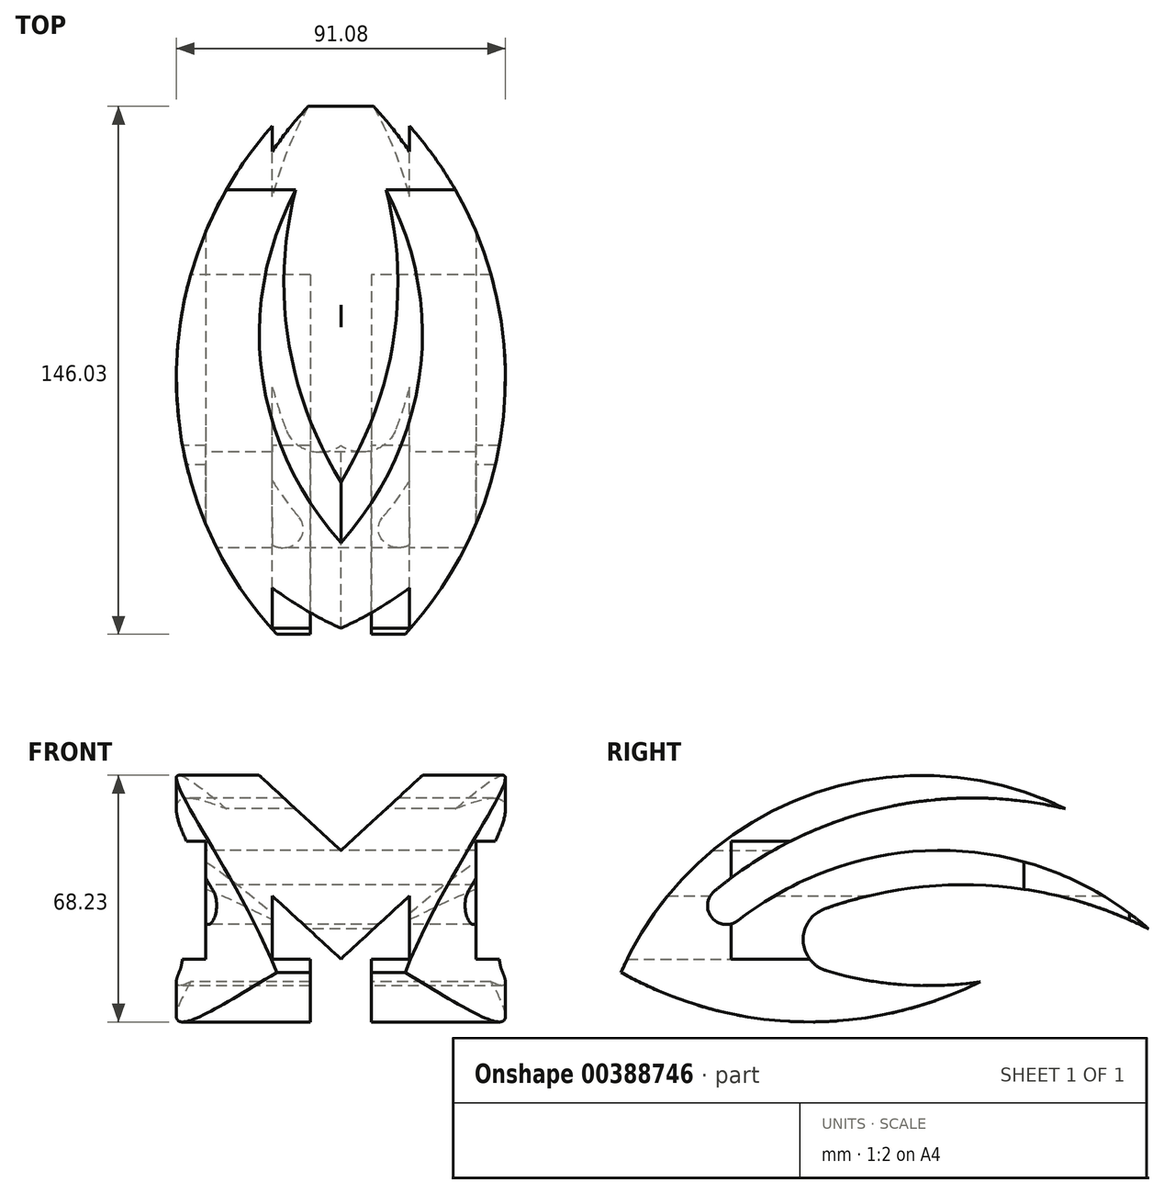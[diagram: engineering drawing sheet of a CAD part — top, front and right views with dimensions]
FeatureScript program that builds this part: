
annotation { "Feature Type Name" : "Feature", "Feature Type Description" : "" }
export const myFeature = defineFeature(function(context is Context, id is Id, definition is map)
    precondition{}
    {
        {
            var Q0;
            Q0=qCreatedBy(makeId("Front.planeOp"),FACE);
            var sketch = newSketch(context, id + "F0", { "sketchPlane" : qUnion([Q0])});
            skLineSegment(sketch, "E0", {"start": v(0, 0) * mm, "end": v(0, 68.23) * mm, "construction": true});
            skLineSegment(sketch, "E1", {"start": v(0, 47.4) * mm, "end": v(-22.61, 68.23) * mm});
            skLineSegment(sketch, "E2", {"start": v(-22.61, 68.23) * mm, "end": v(-45.54, 68.23) * mm});
            skLineSegment(sketch, "E3", {"start": v(-45.54, 68.23) * mm, "end": v(-45.54, 49.97) * mm});
            skLineSegment(sketch, "E4", {"start": v(-45.54, 49.97) * mm, "end": v(-37.38, 49.97) * mm});
            skLineSegment(sketch, "E5", {"start": v(-37.38, 49.97) * mm, "end": v(-37.38, 17.4) * mm});
            skLineSegment(sketch, "E6", {"start": v(-37.38, 17.4) * mm, "end": v(-45.54, 17.4) * mm});
            skLineSegment(sketch, "E7", {"start": v(-45.54, 17.4) * mm, "end": v(-45.54, 0) * mm});
            skLineSegment(sketch, "E8", {"start": v(-45.54, 0) * mm, "end": v(-8.5, 0) * mm});
            skLineSegment(sketch, "E9", {"start": v(-8.5, 0) * mm, "end": v(-8.5, 17.4) * mm});
            skLineSegment(sketch, "E10", {"start": v(-8.5, 17.4) * mm, "end": v(-18.95, 17.4) * mm});
            skLineSegment(sketch, "E11", {"start": v(-18.95, 17.4) * mm, "end": v(-18.95, 34.85) * mm});
            skLineSegment(sketch, "E12", {"start": v(-18.95, 34.85) * mm, "end": v(0, 17.4) * mm});
            skLineSegment(sketch, "E13.MirrorCS", {"start": v(45.54, 49.97) * mm, "end": v(37.38, 49.97) * mm});
            skLineSegment(sketch, "E14.MirrorCS", {"start": v(37.38, 17.4) * mm, "end": v(45.54, 17.4) * mm});
            skLineSegment(sketch, "E15.MirrorCS", {"start": v(8.5, 17.4) * mm, "end": v(18.95, 17.4) * mm});
            skLineSegment(sketch, "E16.MirrorCS", {"start": v(0, 47.4) * mm, "end": v(22.61, 68.23) * mm});
            skLineSegment(sketch, "E17.MirrorCS", {"start": v(18.95, 34.85) * mm, "end": v(0, 17.4) * mm});
            skLineSegment(sketch, "E18.MirrorCS", {"start": v(22.61, 68.23) * mm, "end": v(45.54, 68.23) * mm});
            skLineSegment(sketch, "E19.MirrorCS", {"start": v(45.54, 68.23) * mm, "end": v(45.54, 49.97) * mm});
            skLineSegment(sketch, "E20.MirrorCS", {"start": v(45.54, 0) * mm, "end": v(8.5, 0) * mm});
            skLineSegment(sketch, "E21.MirrorCS", {"start": v(45.54, 17.4) * mm, "end": v(45.54, 0) * mm});
            skLineSegment(sketch, "E22.MirrorCS", {"start": v(18.95, 17.4) * mm, "end": v(18.95, 34.85) * mm});
            skLineSegment(sketch, "E23.MirrorCS", {"start": v(37.38, 49.97) * mm, "end": v(37.38, 17.4) * mm});
            skLineSegment(sketch, "E24.MirrorCS", {"start": v(8.5, 0) * mm, "end": v(8.5, 17.4) * mm});
            skSolve(sketch);
        }
        {
            var Q0;
            Q0 = qSketchRegion(id + "F0", true);
            extrude(context, id + "F1", {"entities" : qUnion([Q0]), "depth" : 170.43 * mm});
        }
        {
            var Q0;
            Q0=makeQuery(id+"F1.opExtrude","SWEPT_FACE",FACE,{"disambiguationData":[OSD([sQuery(id+"F0.wireOp",EDGE,"E3")])]});
            var sketch = newSketch(context, id + "F2", { "sketchPlane" : qUnion([Q0])});
            skArc(sketch, "E25", {"start": v(146.03, 13.7) * mm, "mid": v(94.24, 62.66) * mm, "end": v(23.07, 58.96) * mm});
            skArc(sketch, "E26", {"start": v(46.56, 11.1) * mm, "mid": v(96.62, 0.04) * mm, "end": v(146.03, 13.7) * mm});
            skArc(sketch, "E27", {"start": v(46.56, 11.1) * mm, "mid": v(68.05, 10.3) * mm, "end": v(89.2, 14.17) * mm});
            skArc(sketch, "E28", {"start": v(89.2, 14.17) * mm, "mid": v(95.62, 22.55) * mm, "end": v(89.66, 31.27) * mm});
            skArc(sketch, "E29", {"start": v(89.66, 31.27) * mm, "mid": v(44.26, 37.72) * mm, "end": v(0, 25.72) * mm});
            skArc(sketch, "E30", {"start": v(88.74, 41.9) * mm, "mid": v(42.14, 46.03) * mm, "end": v(0, 25.72) * mm});
            skArc(sketch, "E31", {"start": v(88.74, 41.9) * mm, "mid": v(101.73, 35.9) * mm, "end": v(113.69, 28.03) * mm});
            skArc(sketch, "E32", {"start": v(113.69, 28.03) * mm, "mid": v(120.95, 28.9) * mm, "end": v(120.2, 36.18) * mm});
            skArc(sketch, "E33", {"start": v(120.2, 36.18) * mm, "mid": v(74.32, 59) * mm, "end": v(23.07, 58.96) * mm});
            skSolve(sketch);
        }
        {
            var Q0;
            Q0 = qSketchRegion(id + "F2", true);
            extrude(context, id + "F3", {"entities" : qUnion([Q0]), "operationType" : NewBodyOperationType.INTERSECT, "oppositeDirection" : true, "depth" : 120.14 * mm});
        }
        {
            var Q0;
            Q0=qCreatedBy(makeId("Top.planeOp"),FACE);
            var sketch = newSketch(context, id + "F4", { "sketchPlane" : qUnion([Q0])});
            skArc(sketch, "E34", {"start": v(-13.78, 0) * mm, "mid": v(-45.52, -77.1) * mm, "end": v(-10.8, -152.9) * mm});
            skLineSegment(sketch, "E35", {"start": v(0, 0) * mm, "end": v(0, -164.64) * mm, "construction": true});
            skArc(sketch, "E36.MirrorCS", {"start": v(13.78, 0) * mm, "mid": v(45.52, -77.1) * mm, "end": v(10.8, -152.9) * mm});
            skLineSegment(sketch, "E37", {"start": v(10.8, -152.9) * mm, "end": v(-10.8, -152.9) * mm});
            skLineSegment(sketch, "E38", {"start": v(-13.78, 0) * mm, "end": v(13.78, 0) * mm});
            skSolve(sketch);
        }
        {
            var Q0;
            Q0 = qSketchRegion(id + "F4", true);
            extrude(context, id + "F5", {"entities" : qUnion([Q0]), "operationType" : NewBodyOperationType.INTERSECT, "depth" : 99.57 * mm});
        }
    });
